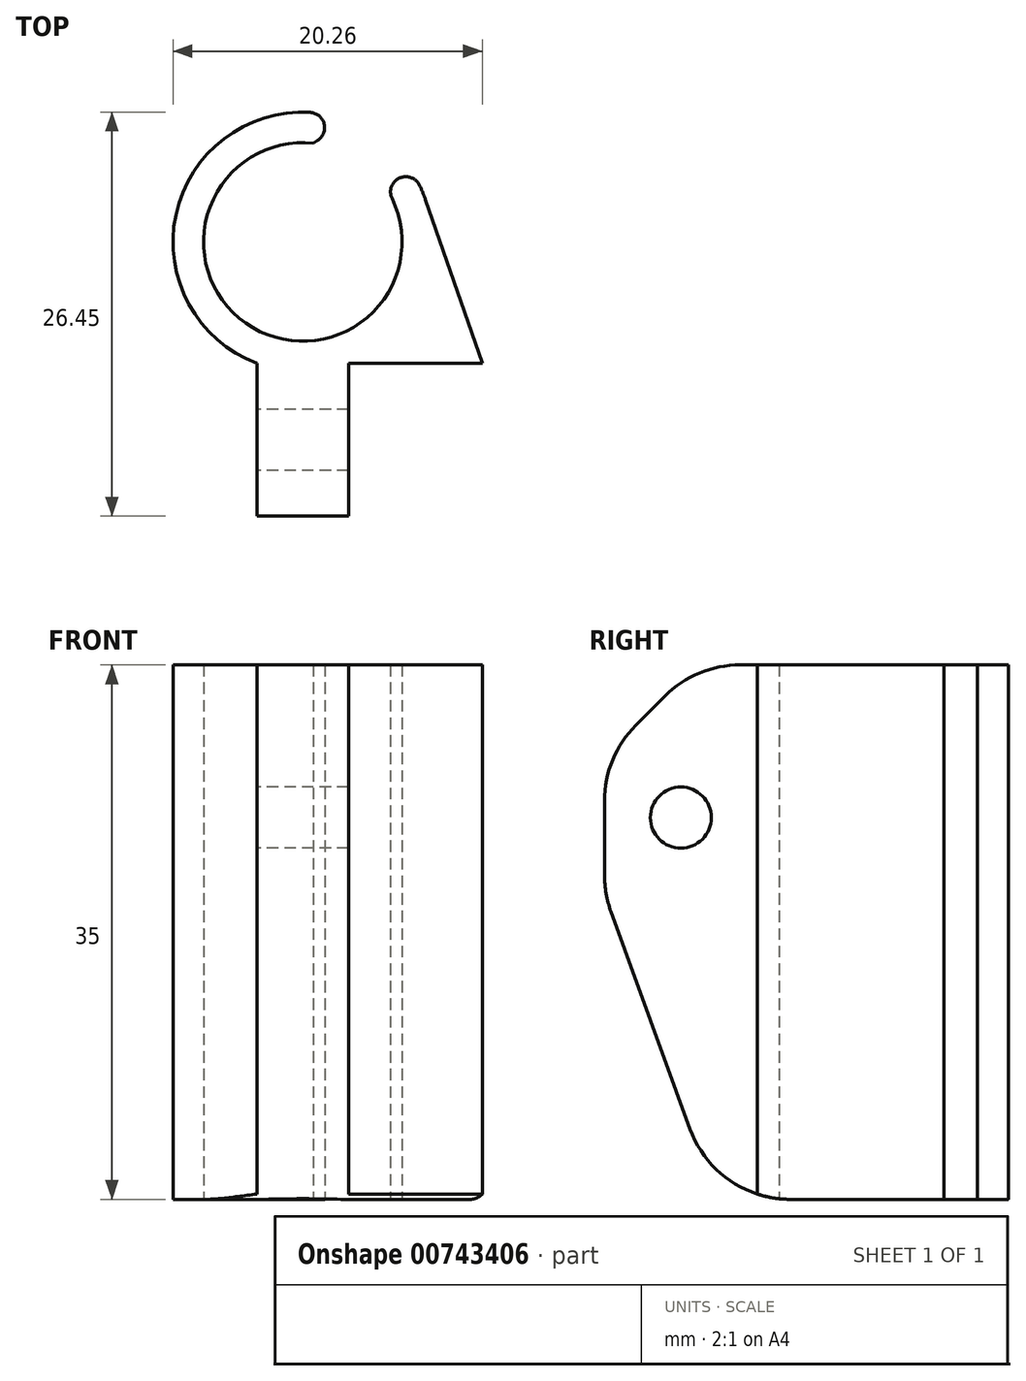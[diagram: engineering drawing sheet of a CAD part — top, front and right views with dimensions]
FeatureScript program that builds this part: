
annotation { "Feature Type Name" : "Feature", "Feature Type Description" : "" }
export const myFeature = defineFeature(function(context is Context, id is Id, definition is map)
    precondition{}
    {
        {
            var Q0;
            Q0=qCreatedBy(makeId("Top.planeOp"),FACE);
            var sketch = newSketch(context, id + "F0", { "sketchPlane" : qUnion([Q0])});
            skLineSegment(sketch, "E0", {"start": v(0, 0) * mm, "end": v(6, 0) * mm});
            skLineSegment(sketch, "E1", {"start": v(6, 0) * mm, "end": v(6, 10) * mm});
            skLineSegment(sketch, "E2", {"start": v(6, 10) * mm, "end": v(14.76, 10) * mm});
            skLineSegment(sketch, "E3", {"start": v(0, 10) * mm, "end": v(0, 0) * mm});
            skCircle(sketch, "E4", {"center": v(3, 17.95) * mm, "radius": 6.5 * mm});
            skCircle(sketch, "E5.0", {"center": v(3, 17.95) * mm, "radius": 8.5 * mm});
            skLineSegment(sketch, "E6", {"start": v(14.76, 10) * mm, "end": v(11.03, 20.74) * mm});
            skLineSegment(sketch, "E7", {"start": v(8.42, 21.55) * mm, "end": v(10.08, 22.65) * mm});
            skLineSegment(sketch, "E8", {"start": v(3.7, 24.42) * mm, "end": v(5.96, 25.92) * mm});
            skSolve(sketch);
        }
        {
            var Q0;
            Q0=makeQuery(id+"F0.imprint","IMPRINT",FACE,{"disambiguationData":[TD([[makeQuery(id+"F0.imprint","IMPRINT",EDGE,{"derivedFrom":sQuery(id+"F0.wireOp",EDGE,"E0")}),1.0]])]});
            var Q1;
            {var subQ0=sQuery(id+"F0.wireOp",EDGE,"E2");Q1=makeQuery(id+"F0.imprint","IMPRINT",FACE,{"disambiguationData":[TD([[makeQuery(id+"F0.imprint","IMPRINT",EDGE,{"derivedFrom":subQ0}),1.0]])]});}
            var Q2;
            {var subQ4=sQuery(id+"F0.wireOp",EDGE,"3sw9NxYT-nd3x-Qu3l-zuWc-8mxZi2qds3Cl");Q2=makeQuery(id+"F0.imprint","IMPRINT",FACE,{"disambiguationData":[TD([[makeQuery(id+"F0.imprint","IMPRINT",EDGE,{"derivedFrom":subQ4}),1.0]])]});}
            var Q3;
            {var subQ5=sQuery(id+"F0.wireOp",EDGE,"E7");Q3=makeQuery(id+"F0.imprint","IMPRINT",FACE,{"disambiguationData":[TD([[makeQuery(id+"F0.imprint","IMPRINT",EDGE,{"derivedFrom":subQ5}),-1.0]])]});}
            extrude(context, id + "F1", {"entities" : qUnion([Q0, Q1, Q2, Q3]), "depth" : 15 * mm, "offsetDistance" : 25 * mm, "hasSecondDirection" : true, "secondDirectionOppositeDirection" : true, "secondDirectionDepth" : 20 * mm});
        }
        {
            var Q0;
            Q0=makeQuery(id+"F1.opExtrude","SWEPT_FACE",FACE,{"disambiguationData":[OSD([sQuery(id+"F0.wireOp",EDGE,"E3")])]});
            var sketch = newSketch(context, id + "F2", { "sketchPlane" : qUnion([Q0])});
            skLineSegment(sketch, "E9.bottom", {"start": v(0, 15) * mm, "end": v(-5, 15) * mm, "construction": true});
            skLineSegment(sketch, "E9.top", {"start": v(0, 5) * mm, "end": v(-5, 5) * mm, "construction": true});
            skLineSegment(sketch, "E9.left", {"start": v(0, 15) * mm, "end": v(0, 5) * mm, "construction": true});
            skLineSegment(sketch, "E9.right", {"start": v(-5, 15) * mm, "end": v(-5, 5) * mm, "construction": true});
            skCircle(sketch, "E10", {"center": v(-5, 5) * mm, "radius": 2 * mm});
            skSolve(sketch);
        }
        {
            var Q0;
            Q0 = qSketchRegion(id + "F2", true);
            extrude(context, id + "F3", {"entities" : qUnion([Q0]), "operationType" : NewBodyOperationType.REMOVE, "endBound" : BoundingType.THROUGH_ALL, "oppositeDirection" : true, "depth" : 25 * mm, "offsetDistance" : 25 * mm});
        }
        {
            var Q0;
            Q0=makeQuery(id+"F1.opExtrude","SWEPT_EDGE",EDGE,{"disambiguationData":[OSD([sQuery(id+"F0.wireOp",EDGE,"E5.0"),sQuery(id+"F0.wireOp",EDGE,"E8")])]});
            var Q1;
            Q1=makeQuery(id+"F1.opExtrude","SWEPT_EDGE",EDGE,{"disambiguationData":[OSD([sQuery(id+"F0.wireOp",EDGE,"E4"),sQuery(id+"F0.wireOp",EDGE,"E7")])]});
            var Q2;
            Q2=makeQuery(id+"F1.opExtrude","SWEPT_EDGE",EDGE,{"disambiguationData":[OSD([sQuery(id+"F0.wireOp",EDGE,"E5.0"),sQuery(id+"F0.wireOp",EDGE,"E7")])]});
            fillet(context, id + "F4", {"entities" : qUnion([Q0, Q1, Q2]), "radius" : 1 * mm, "tangentPropagation" : true, "allowEdgeOverflow" : false});
        }
        {
            var Q0;
            Q0=makeQuery(id+"F1.opExtrude","CAP_EDGE",EDGE,{"disambiguationData":[OSD([sQuery(id+"F0.wireOp",EDGE,"E0")])],"isStart":true});
            chamfer(context, id + "F5", {"entities" : qUnion([Q0]), "chamferType" : ChamferType.OFFSET_ANGLE, "width" : 20 * mm, "oppositeDirection" : false, "angle" : 20 * degree, "tangentPropagation" : true});
        }
        {
            var Q0;
            Q0=makeQuery(id+"F1.opExtrude","CAP_EDGE",EDGE,{"disambiguationData":[OSD([sQuery(id+"F0.wireOp",EDGE,"E0")])],"isStart":false});
            chamfer(context, id + "F6", {"entities" : qUnion([Q0]), "width" : 6 * mm, "tangentPropagation" : true});
        }
        {
            var Q0;
            {var subQ0=sQuery(id+"F0.wireOp",EDGE,"E0");Q0=makeQuery(id+"F6.opChamfer","BLEND_EDGE",EDGE,{"blendedFrom":[makeQuery(id+"F1.opExtrude","CAP_EDGE",EDGE,{"disambiguationData":[OSD([subQ0])],"isStart":false}),makeQuery(id+"F1.opExtrude","SWEPT_FACE",FACE,{"disambiguationData":[OSD([subQ0])]})],"blendedInto":[makeQuery(id+"F1.opExtrude","SWEPT_FACE",FACE,{"disambiguationData":[OSD([subQ0])]})]});}
            var Q1;
            {var subQ0=sQuery(id+"F0.wireOp",EDGE,"E0");Q1=makeQuery(id+"F6.opChamfer","BLEND_EDGE",EDGE,{"blendedFrom":[makeQuery(id+"F1.opExtrude","CAP_EDGE",EDGE,{"disambiguationData":[OSD([subQ0])],"isStart":false}),makeQuery(id+"F1.opExtrude","CAP_FACE",FACE,{"disambiguationData":[OSD([subQ0,sQuery(id+"F0.wireOp",EDGE,"E1"),sQuery(id+"F0.wireOp",EDGE,"E2"),sQuery(id+"F0.wireOp",EDGE,"E3"),sQuery(id+"F0.wireOp",EDGE,"E4"),sQuery(id+"F0.wireOp",EDGE,"E5.0"),sQuery(id+"F0.wireOp",EDGE,"E6"),sQuery(id+"F0.wireOp",EDGE,"E7"),sQuery(id+"F0.wireOp",EDGE,"E8")])],"isStart":false})],"blendedInto":[makeQuery(id+"F1.opExtrude","CAP_FACE",FACE,{"disambiguationData":[OSD([subQ0,sQuery(id+"F0.wireOp",EDGE,"E1"),sQuery(id+"F0.wireOp",EDGE,"E2"),sQuery(id+"F0.wireOp",EDGE,"E3"),sQuery(id+"F0.wireOp",EDGE,"E4"),sQuery(id+"F0.wireOp",EDGE,"E5.0"),sQuery(id+"F0.wireOp",EDGE,"E6"),sQuery(id+"F0.wireOp",EDGE,"E7"),sQuery(id+"F0.wireOp",EDGE,"E8")])],"isStart":false})]});}
            var Q2;
            {var subQ0=sQuery(id+"F0.wireOp",EDGE,"E0");Q2=makeQuery(id+"F5.opChamfer","BLEND_EDGE",EDGE,{"blendedFrom":[makeQuery(id+"F1.opExtrude","CAP_EDGE",EDGE,{"disambiguationData":[OSD([subQ0])],"isStart":true}),makeQuery(id+"F1.opExtrude","CAP_FACE",FACE,{"disambiguationData":[OSD([subQ0,sQuery(id+"F0.wireOp",EDGE,"E1"),sQuery(id+"F0.wireOp",EDGE,"E2"),sQuery(id+"F0.wireOp",EDGE,"E3"),sQuery(id+"F0.wireOp",EDGE,"E4"),sQuery(id+"F0.wireOp",EDGE,"E5.0"),sQuery(id+"F0.wireOp",EDGE,"E6"),sQuery(id+"F0.wireOp",EDGE,"E7"),sQuery(id+"F0.wireOp",EDGE,"E8")])],"isStart":true})],"blendedInto":[makeQuery(id+"F1.opExtrude","CAP_FACE",FACE,{"disambiguationData":[OSD([subQ0,sQuery(id+"F0.wireOp",EDGE,"E1"),sQuery(id+"F0.wireOp",EDGE,"E2"),sQuery(id+"F0.wireOp",EDGE,"E3"),sQuery(id+"F0.wireOp",EDGE,"E4"),sQuery(id+"F0.wireOp",EDGE,"E5.0"),sQuery(id+"F0.wireOp",EDGE,"E6"),sQuery(id+"F0.wireOp",EDGE,"E7"),sQuery(id+"F0.wireOp",EDGE,"E8")])],"isStart":true})]});}
            var Q3;
            {var subQ0=sQuery(id+"F0.wireOp",EDGE,"E0");Q3=makeQuery(id+"F5.opChamfer","BLEND_EDGE",EDGE,{"blendedFrom":[makeQuery(id+"F1.opExtrude","CAP_EDGE",EDGE,{"disambiguationData":[OSD([subQ0])],"isStart":true}),makeQuery(id+"F1.opExtrude","SWEPT_FACE",FACE,{"disambiguationData":[OSD([subQ0])]})],"blendedInto":[makeQuery(id+"F1.opExtrude","SWEPT_FACE",FACE,{"disambiguationData":[OSD([subQ0])]})]});}
            fillet(context, id + "F7", {"entities" : qUnion([Q0, Q1, Q2, Q3]), "radius" : 7 * mm, "tangentPropagation" : true, "allowEdgeOverflow" : false});
        }
    });
